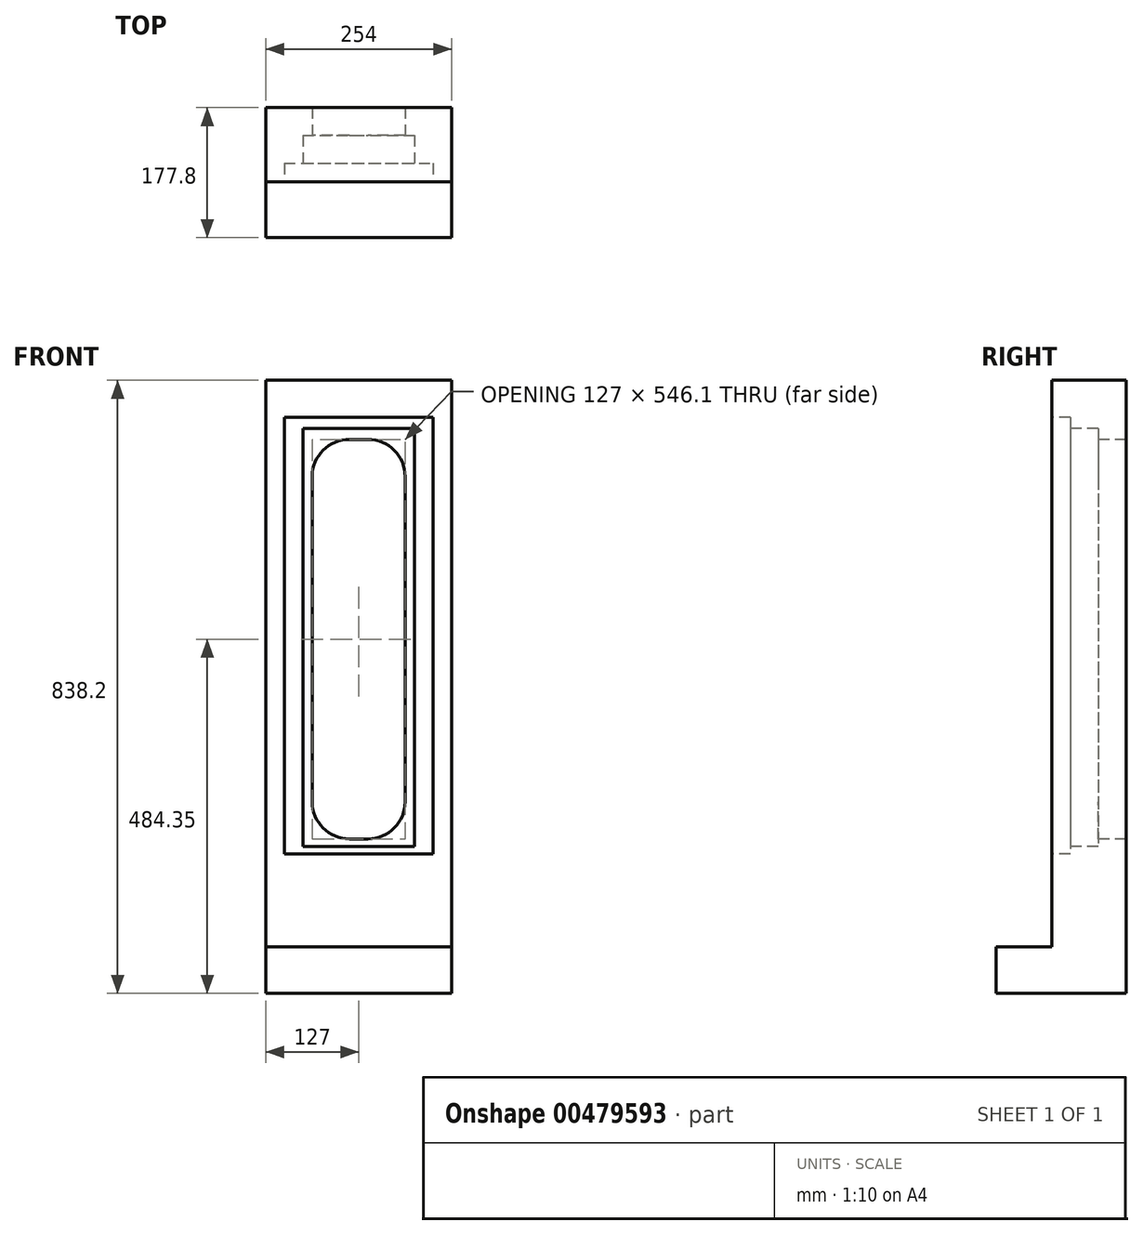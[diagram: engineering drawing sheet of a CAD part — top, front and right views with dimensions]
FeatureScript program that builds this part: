
annotation { "Feature Type Name" : "Feature", "Feature Type Description" : "" }
export const myFeature = defineFeature(function(context is Context, id is Id, definition is map)
    precondition{}
    {
        {
            var Q0;
            Q0=qCreatedBy(makeId("Front.planeOp"),FACE);
            var sketch = newSketch(context, id + "F0", { "sketchPlane" : qUnion([Q0])});
            skLineSegment(sketch, "E0.top", {"start": v(127, 647.7) * mm, "end": v(-127, 647.7) * mm});
            skLineSegment(sketch, "E0.left", {"start": v(127, -190.5) * mm, "end": v(127, 647.7) * mm});
            skLineSegment(sketch, "E0.right", {"start": v(-127, -190.5) * mm, "end": v(-127, 647.7) * mm});
            skPoint(sketch, "E1.middle", {"position": v(0, 0) * mm});
            skLineSegment(sketch, "E2", {"start": v(-127, -190.5) * mm, "end": v(127, -190.5) * mm});
            skPoint(sketch, "E3.orphan", {"position": v(-127, -647.7) * mm});
            skPoint(sketch, "E4.orphan", {"position": v(127, -647.7) * mm});
            skLineSegment(sketch, "E5.bottom", {"start": v(-101.6, 596.9) * mm, "end": v(101.6, 596.9) * mm});
            skLineSegment(sketch, "E5.top", {"start": v(-101.6, 0) * mm, "end": v(101.6, 0) * mm});
            skLineSegment(sketch, "E5.left", {"start": v(-101.6, 596.9) * mm, "end": v(-101.6, 0) * mm});
            skLineSegment(sketch, "E5.right", {"start": v(101.6, 596.9) * mm, "end": v(101.6, 0) * mm});
            skLineSegment(sketch, "E6.bottom", {"start": v(-76.2, 581.9) * mm, "end": v(76.2, 581.9) * mm});
            skLineSegment(sketch, "E6.top", {"start": v(-76.2, 10.4) * mm, "end": v(76.2, 10.4) * mm});
            skLineSegment(sketch, "E6.left", {"start": v(-76.2, 581.9) * mm, "end": v(-76.2, 10.4) * mm});
            skLineSegment(sketch, "E6.right", {"start": v(76.2, 581.9) * mm, "end": v(76.2, 10.4) * mm});
            skLineSegment(sketch, "E7.bottom", {"start": v(-63.5, 566.9) * mm, "end": v(63.5, 566.9) * mm});
            skLineSegment(sketch, "E7.top", {"start": v(-63.5, 20.8) * mm, "end": v(63.5, 20.8) * mm});
            skLineSegment(sketch, "E7.left", {"start": v(-63.5, 566.9) * mm, "end": v(-63.5, 20.8) * mm});
            skLineSegment(sketch, "E7.right", {"start": v(63.5, 566.9) * mm, "end": v(63.5, 20.8) * mm});
            skLineSegment(sketch, "E8", {"start": v(0, 870.13) * mm, "end": v(0, -870.13) * mm, "construction": true});
            skLineSegment(sketch, "E9.top", {"start": v(-127, -127) * mm, "end": v(127, -127) * mm});
            skLineSegment(sketch, "E9.left", {"start": v(-127, -190.5) * mm, "end": v(-127, -127) * mm});
            skLineSegment(sketch, "E9.right", {"start": v(127, -190.5) * mm, "end": v(127, -127) * mm});
            skSolve(sketch);
        }
        {
            var Q0;
            Q0=makeQuery(id+"F0.imprint","IMPRINT",FACE,{"disambiguationData":[TD([[makeQuery(id+"F0.imprint","IMPRINT",EDGE,{"derivedFrom":sQuery(id+"F0.wireOp",EDGE,"E0.top")}),1.0]])]});
            var Q1;
            Q1=makeQuery(id+"F0.imprint","IMPRINT",FACE,{"disambiguationData":[TD([[makeQuery(id+"F0.imprint","IMPRINT",EDGE,{"derivedFrom":sQuery(id+"F0.wireOp",EDGE,"E1.bottom")}),-1.0]])]});
            var Q2;
            Q2=makeQuery(id+"F0.imprint","IMPRINT",FACE,{"disambiguationData":[TD([[makeQuery(id+"F0.imprint","IMPRINT",EDGE,{"derivedFrom":sQuery(id+"F0.wireOp",EDGE,"l2cz76WN-11cX-8Qg5-Wc74-vKwfhGCtYGeO.bottom")}),-1.0]])]});
            var Q3;
            {var subQ0=sQuery(id+"F0.wireOp",EDGE,"dQK7Thth-TP6K-kbBQ-5Cwl-0GHNaYrmpQfn.left");var subQ1=sQuery(id+"F0.wireOp",EDGE,"E1.bottom");var subQ2=makeQuery(id+"F0.imprint","INTERSECT",VERTEX,{"derivedFrom":[subQ1,subQ0]});Q3=makeQuery(id+"F0.imprint","IMPRINT",FACE,{"disambiguationData":[TD([[makeQuery(id+"F0.imprint","IMPRINT",EDGE,{"disambiguationData":[TD([[subQ2,-1.0]])],"derivedFrom":subQ1}),1.0]])]});}
            var Q4;
            {var subQ5=sQuery(id+"F0.wireOp",EDGE,"huDVYpq4-8GHm-f6ov-cYvV-LWDsyoBmHsaB.top");Q4=makeQuery(id+"F0.imprint","IMPRINT",FACE,{"disambiguationData":[TD([[makeQuery(id+"F0.imprint","IMPRINT",EDGE,{"derivedFrom":subQ5}),1.0]])]});}
            var Q5;
            {var subQ5=sQuery(id+"F0.wireOp",EDGE,"dQK7Thth-TP6K-kbBQ-5Cwl-0GHNaYrmpQfn.bottom");Q5=makeQuery(id+"F0.imprint","IMPRINT",FACE,{"disambiguationData":[TD([[makeQuery(id+"F0.imprint","IMPRINT",EDGE,{"derivedFrom":subQ5}),-1.0]])]});}
            var Q6;
            {var subQ5=sQuery(id+"F0.wireOp",EDGE,"dQK7Thth-TP6K-kbBQ-5Cwl-0GHNaYrmpQfn.top");Q6=makeQuery(id+"F0.imprint","IMPRINT",FACE,{"disambiguationData":[TD([[makeQuery(id+"F0.imprint","IMPRINT",EDGE,{"derivedFrom":subQ5}),1.0]])]});}
            var Q7;
            {var subQ5=sQuery(id+"F0.wireOp",EDGE,"huDVYpq4-8GHm-f6ov-cYvV-LWDsyoBmHsaB.bottom");Q7=makeQuery(id+"F0.imprint","IMPRINT",FACE,{"disambiguationData":[TD([[makeQuery(id+"F0.imprint","IMPRINT",EDGE,{"derivedFrom":subQ5}),-1.0]])]});}
            var Q8;
            {var subQ0=sQuery(id+"F0.wireOp",EDGE,"dQK7Thth-TP6K-kbBQ-5Cwl-0GHNaYrmpQfn.left");var subQ1=sQuery(id+"F0.wireOp",EDGE,"E1.bottom");var subQ2=makeQuery(id+"F0.imprint","INTERSECT",VERTEX,{"derivedFrom":[subQ1,subQ0]});Q8=makeQuery(id+"F0.imprint","IMPRINT",FACE,{"disambiguationData":[TD([[makeQuery(id+"F0.imprint","IMPRINT",EDGE,{"disambiguationData":[TD([[subQ2,-1.0]])],"derivedFrom":subQ1}),-1.0]])]});}
            var Q9;
            Q9=makeQuery(id+"F0.imprint","IMPRINT",FACE,{"disambiguationData":[TD([[makeQuery(id+"F0.imprint","IMPRINT",EDGE,{"derivedFrom":sQuery(id+"F0.wireOp",EDGE,"E6.bottom")}),-1.0]])]});
            var Q10;
            Q10=makeQuery(id+"F0.imprint","IMPRINT",FACE,{"disambiguationData":[TD([[makeQuery(id+"F0.imprint","IMPRINT",EDGE,{"derivedFrom":sQuery(id+"F0.wireOp",EDGE,"E5.bottom")}),-1.0]])]});
            var Q11;
            Q11=makeQuery(id+"F0.imprint","IMPRINT",FACE,{"disambiguationData":[TD([[makeQuery(id+"F0.imprint","IMPRINT",EDGE,{"derivedFrom":sQuery(id+"F0.wireOp",EDGE,"E2")}),1.0]])]});
            extrude(context, id + "F1", {"entities" : qUnion([Q0, Q1, Q2, Q3, Q4, Q5, Q6, Q7, Q8, Q9, Q10, Q11]), "oppositeDirection" : true, "depth" : 101.6 * mm});
        }
        {
            var Q0;
            Q0=makeQuery(id+"F0.imprint","IMPRINT",FACE,{"disambiguationData":[TD([[makeQuery(id+"F0.imprint","IMPRINT",EDGE,{"derivedFrom":sQuery(id+"F0.wireOp",EDGE,"E5.bottom")}),-1.0]])]});
            extrude(context, id + "F2", {"entities" : qUnion([Q0]), "operationType" : NewBodyOperationType.REMOVE, "oppositeDirection" : true, "depth" : 25.4 * mm});
        }
        {
            var Q0;
            Q0=makeQuery(id+"F0.imprint","IMPRINT",FACE,{"disambiguationData":[TD([[makeQuery(id+"F0.imprint","IMPRINT",EDGE,{"derivedFrom":sQuery(id+"F0.wireOp",EDGE,"E6.bottom")}),-1.0]])]});
            extrude(context, id + "F3", {"entities" : qUnion([Q0]), "operationType" : NewBodyOperationType.REMOVE, "oppositeDirection" : true, "depth" : 63.5 * mm});
        }
        {
            var Q0;
            Q0=makeQuery(id+"F1.opExtrude","SWEPT_EDGE",EDGE,{"disambiguationData":[OSD([sQuery(id+"F0.wireOp",EDGE,"E7.bottom"),sQuery(id+"F0.wireOp",EDGE,"E7.right")])]});
            var Q1;
            Q1=makeQuery(id+"F1.opExtrude","SWEPT_EDGE",EDGE,{"disambiguationData":[OSD([sQuery(id+"F0.wireOp",EDGE,"E7.bottom"),sQuery(id+"F0.wireOp",EDGE,"E7.left")])]});
            var Q2;
            Q2=makeQuery(id+"F1.opExtrude","SWEPT_EDGE",EDGE,{"disambiguationData":[OSD([sQuery(id+"F0.wireOp",EDGE,"E7.top"),sQuery(id+"F0.wireOp",EDGE,"E7.left")])]});
            var Q3;
            Q3=makeQuery(id+"F1.opExtrude","SWEPT_EDGE",EDGE,{"disambiguationData":[OSD([sQuery(id+"F0.wireOp",EDGE,"E7.top"),sQuery(id+"F0.wireOp",EDGE,"E7.right")])]});
            fillet(context, id + "F4", {"entities" : qUnion([Q0, Q1, Q2, Q3]), "radius" : 50.8 * mm, "tangentPropagation" : true, "allowEdgeOverflow" : false});
        }
        {
            var Q0;
            Q0=makeQuery(id+"F0.imprint","IMPRINT",FACE,{"disambiguationData":[TD([[makeQuery(id+"F0.imprint","IMPRINT",EDGE,{"derivedFrom":sQuery(id+"F0.wireOp",EDGE,"E2")}),1.0]])]});
            extrude(context, id + "F5", {"entities" : qUnion([Q0]), "operationType" : NewBodyOperationType.ADD, "depth" : 76.2 * mm});
        }
    });
